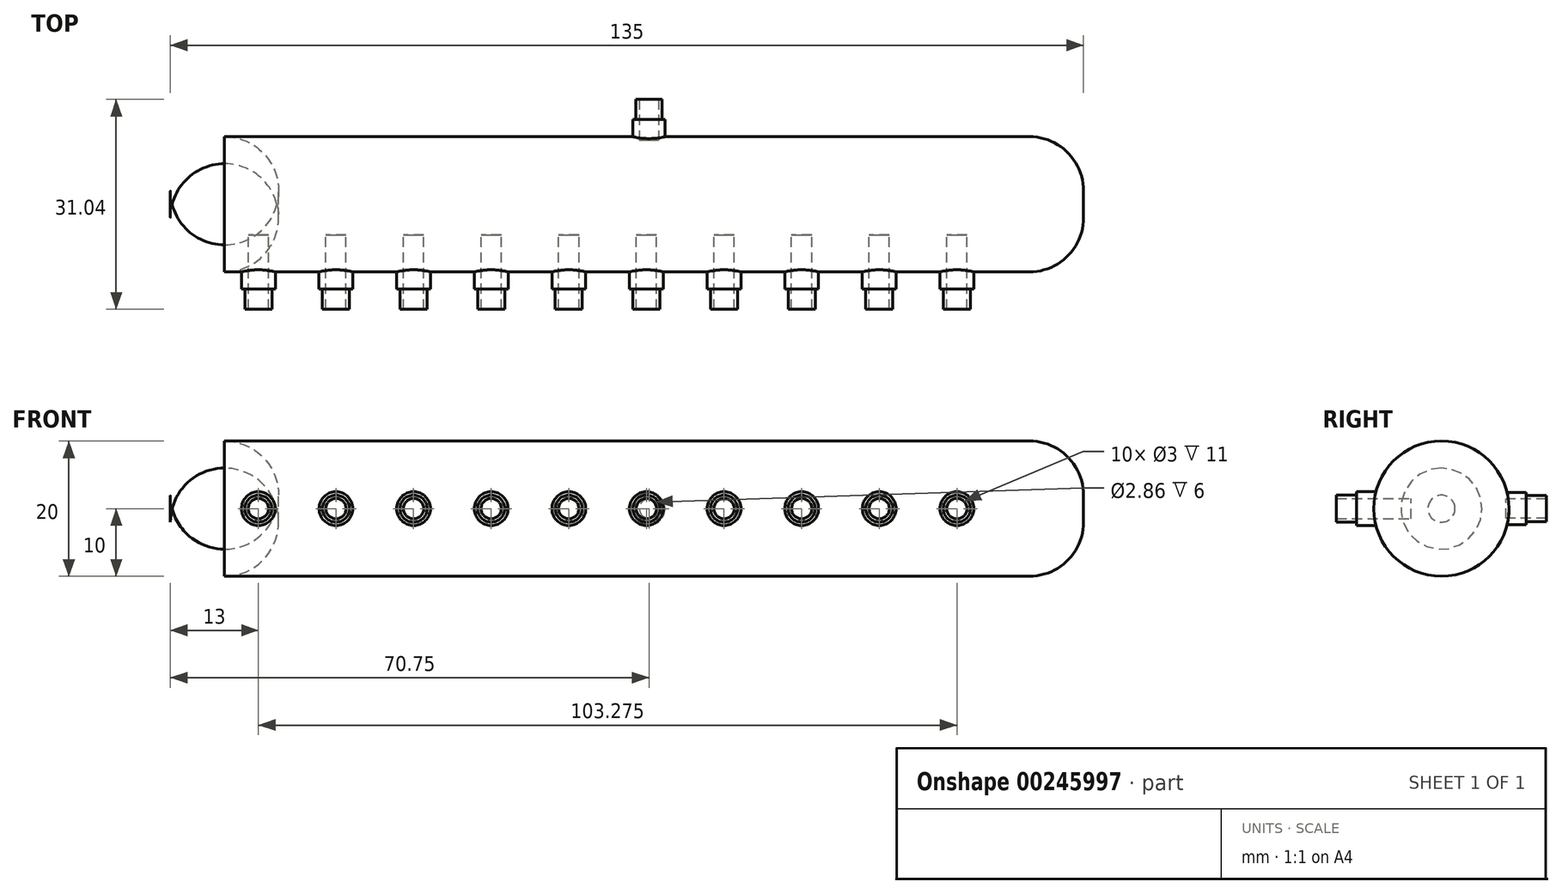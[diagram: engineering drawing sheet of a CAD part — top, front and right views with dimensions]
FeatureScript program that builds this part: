
annotation { "Feature Type Name" : "Feature", "Feature Type Description" : "" }
export const myFeature = defineFeature(function(context is Context, id is Id, definition is map)
    precondition{}
    {
        {
            assignVariable(context, id + "F0", {"name" : "big_radius", "anyValue" : 20});
        }
        {
            assignVariable(context, id + "F1", {"name" : "tube_length", "anyValue" : 135});
        }
        {
            var Q0;
            Q0=qCreatedBy(makeId("Right.planeOp"),FACE);
            var sketch = newSketch(context, id + "F2", { "sketchPlane" : qUnion([Q0])});
            skCircle(sketch, "E0", {"center": v(0, 0) * mm, "radius": 10 * mm});
            skLineSegment(sketch, "E1", {"start": v(-10, 0) * mm, "end": v(-10, 26.48) * mm, "construction": true});
            skSolve(sketch);
        }
        {
            var Q0;
            Q0=makeQuery(id+"F2.imprint","IMPRINT",FACE,{"disambiguationData":[TD([[makeQuery(id+"F2.imprint","IMPRINT",EDGE,{"derivedFrom":sQuery(id+"F2.wireOp",EDGE,"E0")}),1.0]])]});
            extrude(context, id + "F3", {"entities" : qUnion([Q0]), "depth" : (getVariable(context, 'tube_length')) * mm, "offsetDistance" : 25 * mm});
        }
        {
            var Q0;
            Q0=makeQuery(id+"F3.opExtrude","CAP_FACE",FACE,{"disambiguationData":[OSD([sQuery(id+"F2.wireOp",EDGE,"E0")])],"isStart":false});
            fillet(context, id + "F4", {"entities" : qUnion([Q0]), "radius" : 8 * mm, "tangentPropagation" : true, "allowEdgeOverflow" : false});
        }
        {
            var Q0;
            Q0=makeQuery(id+"F3.opExtrude","CAP_FACE",FACE,{"disambiguationData":[OSD([sQuery(id+"F2.wireOp",EDGE,"E0")])],"isStart":true});
            fillet(context, id + "F5", {"entities" : qUnion([Q0]), "radius" : 8 * mm, "tangentPropagation" : true, "allowEdgeOverflow" : false});
        }
        {
            var Q0;
            Q0=qCreatedBy(makeId("Front.planeOp"),FACE);
            cPlane(context, id + "F6", {"entities" : qUnion([Q0]), "cplaneType" : CPlaneType.OFFSET, "offset" : (getVariable(context, 'big_radius') / 2.1) * mm, "width" : 150 * mm, "height" : 150 * mm});
        }
        {
            var Q0;
            Q0=qCreatedBy(id+"F6.planeOp",FACE);
            var sketch = newSketch(context, id + "F7", { "sketchPlane" : qUnion([Q0])});
            skCircle(sketch, "E2", {"center": v(13, 0) * mm, "radius": 2.5 * mm});
            skCircle(sketch, "E3.0", {"center": v(13, 0) * mm, "radius": 1.5 * mm});
            skCircle(sketch, "E4.1.0.0", {"center": v(24.48, 0) * mm, "radius": 1.5 * mm});
            skCircle(sketch, "E4.1.0.1", {"center": v(24.48, 0) * mm, "radius": 2.5 * mm});
            skCircle(sketch, "E4.2.0.0", {"center": v(35.95, 0) * mm, "radius": 1.5 * mm});
            skCircle(sketch, "E4.2.0.1", {"center": v(35.95, 0) * mm, "radius": 2.5 * mm});
            skCircle(sketch, "E4.3.0.0", {"center": v(47.43, 0) * mm, "radius": 1.5 * mm});
            skCircle(sketch, "E4.3.0.1", {"center": v(47.43, 0) * mm, "radius": 2.5 * mm});
            skCircle(sketch, "E4.4.0.0", {"center": v(58.9, 0) * mm, "radius": 1.5 * mm});
            skCircle(sketch, "E4.4.0.1", {"center": v(58.9, 0) * mm, "radius": 2.5 * mm});
            skCircle(sketch, "E4.5.0.0", {"center": v(70.38, 0) * mm, "radius": 1.5 * mm});
            skCircle(sketch, "E4.5.0.1", {"center": v(70.38, 0) * mm, "radius": 2.5 * mm});
            skCircle(sketch, "E4.6.0.0", {"center": v(81.85, 0) * mm, "radius": 1.5 * mm});
            skCircle(sketch, "E4.6.0.1", {"center": v(81.85, 0) * mm, "radius": 2.5 * mm});
            skCircle(sketch, "E4.7.0.0", {"center": v(93.33, 0) * mm, "radius": 1.5 * mm});
            skCircle(sketch, "E4.7.0.1", {"center": v(93.33, 0) * mm, "radius": 2.5 * mm});
            skCircle(sketch, "E4.8.0.0", {"center": v(104.8, 0) * mm, "radius": 1.5 * mm});
            skCircle(sketch, "E4.8.0.1", {"center": v(104.8, 0) * mm, "radius": 2.5 * mm});
            skCircle(sketch, "E4.9.0.0", {"center": v(116.28, 0) * mm, "radius": 1.5 * mm});
            skCircle(sketch, "E4.9.0.1", {"center": v(116.28, 0) * mm, "radius": 2.5 * mm});
            skLineSegment(sketch, "E4.direction1", {"start": v(13, 0) * mm, "end": v(24.48, 0) * mm, "construction": true});
            skSolve(sketch);
        }
        {
            var Q0;
            Q0=makeQuery(id+"F7.imprint","IMPRINT",FACE,{"disambiguationData":[TD([[makeQuery(id+"F7.imprint","IMPRINT",EDGE,{"derivedFrom":sQuery(id+"F7.wireOp",EDGE,"E2")}),1.0]])]});
            var Q1;
            Q1=makeQuery(id+"F7.imprint","IMPRINT",FACE,{"disambiguationData":[TD([[makeQuery(id+"F7.imprint","IMPRINT",EDGE,{"derivedFrom":sQuery(id+"F7.wireOp",EDGE,"E4.1.0.0")}),-1.0]])]});
            var Q2;
            Q2=makeQuery(id+"F7.imprint","IMPRINT",FACE,{"disambiguationData":[TD([[makeQuery(id+"F7.imprint","IMPRINT",EDGE,{"derivedFrom":sQuery(id+"F7.wireOp",EDGE,"E4.2.0.0")}),-1.0]])]});
            var Q3;
            Q3=makeQuery(id+"F7.imprint","IMPRINT",FACE,{"disambiguationData":[TD([[makeQuery(id+"F7.imprint","IMPRINT",EDGE,{"derivedFrom":sQuery(id+"F7.wireOp",EDGE,"E4.3.0.0")}),-1.0]])]});
            var Q4;
            Q4=makeQuery(id+"F7.imprint","IMPRINT",FACE,{"disambiguationData":[TD([[makeQuery(id+"F7.imprint","IMPRINT",EDGE,{"derivedFrom":sQuery(id+"F7.wireOp",EDGE,"E4.4.0.0")}),-1.0]])]});
            var Q5;
            Q5=makeQuery(id+"F7.imprint","IMPRINT",FACE,{"disambiguationData":[TD([[makeQuery(id+"F7.imprint","IMPRINT",EDGE,{"derivedFrom":sQuery(id+"F7.wireOp",EDGE,"E4.5.0.0")}),-1.0]])]});
            var Q6;
            Q6=makeQuery(id+"F7.imprint","IMPRINT",FACE,{"disambiguationData":[TD([[makeQuery(id+"F7.imprint","IMPRINT",EDGE,{"derivedFrom":sQuery(id+"F7.wireOp",EDGE,"E4.6.0.0")}),-1.0]])]});
            var Q7;
            Q7=makeQuery(id+"F7.imprint","IMPRINT",FACE,{"disambiguationData":[TD([[makeQuery(id+"F7.imprint","IMPRINT",EDGE,{"derivedFrom":sQuery(id+"F7.wireOp",EDGE,"E4.7.0.0")}),-1.0]])]});
            var Q8;
            Q8=makeQuery(id+"F7.imprint","IMPRINT",FACE,{"disambiguationData":[TD([[makeQuery(id+"F7.imprint","IMPRINT",EDGE,{"derivedFrom":sQuery(id+"F7.wireOp",EDGE,"E4.8.0.0")}),-1.0]])]});
            var Q9;
            Q9=makeQuery(id+"F7.imprint","IMPRINT",FACE,{"disambiguationData":[TD([[makeQuery(id+"F7.imprint","IMPRINT",EDGE,{"derivedFrom":sQuery(id+"F7.wireOp",EDGE,"E4.9.0.0")}),-1.0]])]});
            extrude(context, id + "F8", {"entities" : qUnion([Q0, Q1, Q2, Q3, Q4, Q5, Q6, Q7, Q8, Q9]), "operationType" : NewBodyOperationType.ADD, "depth" : 3 * mm, "offsetDistance" : 25 * mm});
        }
        {
            var Q0;
            Q0=makeQuery(id+"F7.imprint","IMPRINT",FACE,{"disambiguationData":[TD([[makeQuery(id+"F7.imprint","IMPRINT",EDGE,{"derivedFrom":sQuery(id+"F7.wireOp",EDGE,"E3.0")}),1.0]])]});
            var Q1;
            Q1=makeQuery(id+"F7.imprint","IMPRINT",FACE,{"disambiguationData":[TD([[makeQuery(id+"F7.imprint","IMPRINT",EDGE,{"derivedFrom":sQuery(id+"F7.wireOp",EDGE,"E4.1.0.0")}),1.0]])]});
            var Q2;
            Q2=makeQuery(id+"F7.imprint","IMPRINT",FACE,{"disambiguationData":[TD([[makeQuery(id+"F7.imprint","IMPRINT",EDGE,{"derivedFrom":sQuery(id+"F7.wireOp",EDGE,"E4.2.0.0")}),1.0]])]});
            var Q3;
            Q3=makeQuery(id+"F7.imprint","IMPRINT",FACE,{"disambiguationData":[TD([[makeQuery(id+"F7.imprint","IMPRINT",EDGE,{"derivedFrom":sQuery(id+"F7.wireOp",EDGE,"E4.3.0.0")}),1.0]])]});
            var Q4;
            Q4=makeQuery(id+"F7.imprint","IMPRINT",FACE,{"disambiguationData":[TD([[makeQuery(id+"F7.imprint","IMPRINT",EDGE,{"derivedFrom":sQuery(id+"F7.wireOp",EDGE,"E4.4.0.0")}),1.0]])]});
            var Q5;
            Q5=makeQuery(id+"F7.imprint","IMPRINT",FACE,{"disambiguationData":[TD([[makeQuery(id+"F7.imprint","IMPRINT",EDGE,{"derivedFrom":sQuery(id+"F7.wireOp",EDGE,"E4.5.0.0")}),1.0]])]});
            var Q6;
            Q6=makeQuery(id+"F7.imprint","IMPRINT",FACE,{"disambiguationData":[TD([[makeQuery(id+"F7.imprint","IMPRINT",EDGE,{"derivedFrom":sQuery(id+"F7.wireOp",EDGE,"E4.6.0.0")}),1.0]])]});
            var Q7;
            Q7=makeQuery(id+"F7.imprint","IMPRINT",FACE,{"disambiguationData":[TD([[makeQuery(id+"F7.imprint","IMPRINT",EDGE,{"derivedFrom":sQuery(id+"F7.wireOp",EDGE,"E4.7.0.0")}),1.0]])]});
            var Q8;
            Q8=makeQuery(id+"F7.imprint","IMPRINT",FACE,{"disambiguationData":[TD([[makeQuery(id+"F7.imprint","IMPRINT",EDGE,{"derivedFrom":sQuery(id+"F7.wireOp",EDGE,"E4.8.0.0")}),1.0]])]});
            var Q9;
            Q9=makeQuery(id+"F7.imprint","IMPRINT",FACE,{"disambiguationData":[TD([[makeQuery(id+"F7.imprint","IMPRINT",EDGE,{"derivedFrom":sQuery(id+"F7.wireOp",EDGE,"E4.9.0.0")}),1.0]])]});
            extrude(context, id + "F9", {"entities" : qUnion([Q0, Q1, Q2, Q3, Q4, Q5, Q6, Q7, Q8, Q9]), "operationType" : NewBodyOperationType.REMOVE, "oppositeDirection" : true, "depth" : 10 * mm, "offsetDistance" : 25 * mm, "symmetric" : true});
        }
        {
            var Q0;
            Q0=qCreatedBy(makeId("Front.planeOp"),FACE);
            cPlane(context, id + "F10", {"entities" : qUnion([Q0]), "cplaneType" : CPlaneType.OFFSET, "offset" : (getVariable(context, 'big_radius') / 2.1) * mm, "oppositeDirection" : true, "width" : 150 * mm, "height" : 150 * mm});
        }
        {
            var Q0;
            Q0=qCreatedBy(id+"F10.planeOp",FACE);
            var sketch = newSketch(context, id + "F11", { "sketchPlane" : qUnion([Q0])});
            skCircle(sketch, "E5.0", {"center": v(70.75, 0) * mm, "radius": 2.38 * mm});
            skCircle(sketch, "E5.1", {"center": v(70.75, 0) * mm, "radius": 1.43 * mm});
            skSolve(sketch);
        }
        {
            var Q0;
            Q0=makeQuery(id+"F11.imprint","IMPRINT",FACE,{"disambiguationData":[TD([[makeQuery(id+"F11.imprint","IMPRINT",EDGE,{"derivedFrom":sQuery(id+"F11.wireOp",EDGE,"E5.1")}),1.0]])]});
            extrude(context, id + "F12", {"entities" : qUnion([Q0]), "operationType" : NewBodyOperationType.REMOVE, "oppositeDirection" : true, "depth" : 10 * mm, "offsetDistance" : 25 * mm});
        }
        {
            var Q0;
            Q0=makeQuery(id+"F11.imprint","IMPRINT",FACE,{"disambiguationData":[TD([[makeQuery(id+"F11.imprint","IMPRINT",EDGE,{"derivedFrom":sQuery(id+"F11.wireOp",EDGE,"E5.0")}),1.0]])]});
            extrude(context, id + "F13", {"entities" : qUnion([Q0]), "operationType" : NewBodyOperationType.ADD, "oppositeDirection" : true, "depth" : 3 * mm, "offsetDistance" : 25 * mm});
        }
        {
            var Q0;
            Q0=makeQuery(id+"F8.opExtrude","CAP_FACE",FACE,{"disambiguationData":[OSD([sQuery(id+"F7.wireOp",EDGE,"E2"),sQuery(id+"F7.wireOp",EDGE,"E3.0")])],"isStart":false});
            var sketch = newSketch(context, id + "F14", { "sketchPlane" : qUnion([Q0])});
            skCircle(sketch, "E6.0", {"center": v(13, 0) * mm, "radius": 1.5 * mm});
            skCircle(sketch, "E7.0", {"center": v(13, 0) * mm, "radius": 2 * mm});
            skCircle(sketch, "E8.1.0.0", {"center": v(24.47, 0) * mm, "radius": 1.5 * mm});
            skCircle(sketch, "E8.1.0.1", {"center": v(24.47, 0) * mm, "radius": 2 * mm});
            skCircle(sketch, "E8.2.0.0", {"center": v(35.95, 0) * mm, "radius": 1.5 * mm});
            skCircle(sketch, "E8.2.0.1", {"center": v(35.95, 0) * mm, "radius": 2 * mm});
            skCircle(sketch, "E8.3.0.0", {"center": v(47.42, 0) * mm, "radius": 1.5 * mm});
            skCircle(sketch, "E8.3.0.1", {"center": v(47.42, 0) * mm, "radius": 2 * mm});
            skCircle(sketch, "E8.4.0.0", {"center": v(58.9, 0) * mm, "radius": 1.5 * mm});
            skCircle(sketch, "E8.4.0.1", {"center": v(58.9, 0) * mm, "radius": 2 * mm});
            skCircle(sketch, "E8.5.0.0", {"center": v(70.38, 0) * mm, "radius": 1.5 * mm});
            skCircle(sketch, "E8.5.0.1", {"center": v(70.38, 0) * mm, "radius": 2 * mm});
            skCircle(sketch, "E8.6.0.0", {"center": v(81.85, 0) * mm, "radius": 1.5 * mm});
            skCircle(sketch, "E8.6.0.1", {"center": v(81.85, 0) * mm, "radius": 2 * mm});
            skCircle(sketch, "E8.7.0.0", {"center": v(93.32, 0) * mm, "radius": 1.5 * mm});
            skCircle(sketch, "E8.7.0.1", {"center": v(93.32, 0) * mm, "radius": 2 * mm});
            skCircle(sketch, "E8.8.0.0", {"center": v(104.8, 0) * mm, "radius": 1.5 * mm});
            skCircle(sketch, "E8.8.0.1", {"center": v(104.8, 0) * mm, "radius": 2 * mm});
            skCircle(sketch, "E8.9.0.0", {"center": v(116.27, 0) * mm, "radius": 1.5 * mm});
            skCircle(sketch, "E8.9.0.1", {"center": v(116.27, 0) * mm, "radius": 2 * mm});
            skLineSegment(sketch, "E8.direction1", {"start": v(13, 0) * mm, "end": v(24.47, 0) * mm, "construction": true});
            skSolve(sketch);
        }
        {
            var Q0;
            Q0=makeQuery(id+"F14.imprint","IMPRINT",FACE,{"disambiguationData":[TD([[makeQuery(id+"F14.imprint","IMPRINT",EDGE,{"derivedFrom":sQuery(id+"F14.wireOp",EDGE,"E6.0")}),-1.0]])]});
            var Q1;
            Q1=makeQuery(id+"F14.imprint","IMPRINT",FACE,{"disambiguationData":[TD([[makeQuery(id+"F14.imprint","IMPRINT",EDGE,{"derivedFrom":sQuery(id+"F14.wireOp",EDGE,"E8.1.0.0")}),-1.0]])]});
            var Q2;
            Q2=makeQuery(id+"F14.imprint","IMPRINT",FACE,{"disambiguationData":[TD([[makeQuery(id+"F14.imprint","IMPRINT",EDGE,{"derivedFrom":sQuery(id+"F14.wireOp",EDGE,"E8.2.0.0")}),-1.0]])]});
            var Q3;
            Q3=makeQuery(id+"F14.imprint","IMPRINT",FACE,{"disambiguationData":[TD([[makeQuery(id+"F14.imprint","IMPRINT",EDGE,{"derivedFrom":sQuery(id+"F14.wireOp",EDGE,"E8.3.0.0")}),-1.0]])]});
            var Q4;
            Q4=makeQuery(id+"F14.imprint","IMPRINT",FACE,{"disambiguationData":[TD([[makeQuery(id+"F14.imprint","IMPRINT",EDGE,{"derivedFrom":sQuery(id+"F14.wireOp",EDGE,"E8.4.0.0")}),-1.0]])]});
            var Q5;
            Q5=makeQuery(id+"F14.imprint","IMPRINT",FACE,{"disambiguationData":[TD([[makeQuery(id+"F14.imprint","IMPRINT",EDGE,{"derivedFrom":sQuery(id+"F14.wireOp",EDGE,"E8.5.0.0")}),-1.0]])]});
            var Q6;
            Q6=makeQuery(id+"F14.imprint","IMPRINT",FACE,{"disambiguationData":[TD([[makeQuery(id+"F14.imprint","IMPRINT",EDGE,{"derivedFrom":sQuery(id+"F14.wireOp",EDGE,"E8.6.0.0")}),-1.0]])]});
            var Q7;
            Q7=makeQuery(id+"F14.imprint","IMPRINT",FACE,{"disambiguationData":[TD([[makeQuery(id+"F14.imprint","IMPRINT",EDGE,{"derivedFrom":sQuery(id+"F14.wireOp",EDGE,"E8.7.0.0")}),-1.0]])]});
            var Q8;
            Q8=makeQuery(id+"F14.imprint","IMPRINT",FACE,{"disambiguationData":[TD([[makeQuery(id+"F14.imprint","IMPRINT",EDGE,{"derivedFrom":sQuery(id+"F14.wireOp",EDGE,"E8.8.0.0")}),-1.0]])]});
            var Q9;
            Q9=makeQuery(id+"F14.imprint","IMPRINT",FACE,{"disambiguationData":[TD([[makeQuery(id+"F14.imprint","IMPRINT",EDGE,{"derivedFrom":sQuery(id+"F14.wireOp",EDGE,"E8.9.0.0")}),-1.0]])]});
            extrude(context, id + "F15", {"entities" : qUnion([Q0, Q1, Q2, Q3, Q4, Q5, Q6, Q7, Q8, Q9]), "operationType" : NewBodyOperationType.ADD, "depth" : 3 * mm, "offsetDistance" : 25 * mm});
        }
        {
            var Q0;
            Q0=makeQuery(id+"F13.opExtrude","CAP_FACE",FACE,{"disambiguationData":[OSD([sQuery(id+"F11.wireOp",EDGE,"E5.0"),sQuery(id+"F11.wireOp",EDGE,"E5.1")])],"isStart":false});
            var sketch = newSketch(context, id + "F16", { "sketchPlane" : qUnion([Q0])});
            skCircle(sketch, "E9.0", {"center": v(-70.75, 0) * mm, "radius": 1.43 * mm});
            skCircle(sketch, "E10.0", {"center": v(-70.75, 0) * mm, "radius": 1.93 * mm});
            skSolve(sketch);
        }
        {
            var Q0;
            Q0=makeQuery(id+"F16.imprint","IMPRINT",FACE,{"disambiguationData":[TD([[makeQuery(id+"F16.imprint","IMPRINT",EDGE,{"derivedFrom":sQuery(id+"F16.wireOp",EDGE,"E9.0")}),1.0]])]});
            extrude(context, id + "F17", {"entities" : qUnion([Q0]), "operationType" : NewBodyOperationType.ADD, "depth" : 3 * mm, "offsetDistance" : 25 * mm});
        }
    });
